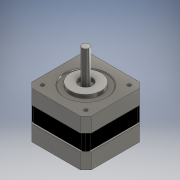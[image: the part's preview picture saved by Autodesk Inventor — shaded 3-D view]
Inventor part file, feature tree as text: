
AUTODESK INVENTOR PART (.ipt)
format: ipt  version: 2016 (Build 200138000, 138)  size: 325,632 bytes
history: native  units: mm
features: sketch x8, extrude x7, chamfer x2, other x1, fillet x1
ambient origin geometry x8: Origin, YZ Plane, XZ Plane, XY Plane, X Axis, Y Axis, Z Axis, Center Point
bodies: Solid1 (feature_tree), Body (feature_tree)
feature tree (19):
  extrude  "Raised"  Depth=42.0mm
  extrude  "Axle"  Depth=27.0mm
  extrude  "Face Indent"  Depth=27.0mm
  chamfer  "Indent Chamf"  Distance=2.5mm
  extrude  "Power Base"  Depth=2.5mm
  extrude  "Power Adapter"  Depth=33.0mm TaperAngle=0.0deg
  other  "Motor Center"
  extrude  "Coil/Winding"  Depth=22.0mm
  fillet  "Cleaner Edges"  Radius=2.0mm
  extrude  "Axle Cap"  Depth=2.0mm
  chamfer  "Cleaner Back Axle"  Distance=22.0mm
  sketch  "Sketch1"  dims[d0=42.0mm d1=42.0mm]
  sketch  "Sketch2"  dims[d2=27.0mm d3=27.0mm]
  sketch  "Sketch3"  dims[d4=27.0mm d5=27.0mm]
  sketch  "Sketch4"  dims[d18=34.367532mm]
  sketch  "Sketch5"  dims[d19=30.75mm]
  sketch  "Sketch6"  dims[d20=30.75mm]
  sketch  "Sketch7"  dims[d21=2.5mm]
  sketch  "Sketch8"  dims[d22=2.5mm d23=2.5mm d24=2.5mm d25=33.0mm d26=0.0mm d27=22.0mm d28=2.0mm d29=0.0mm d30=5.0mm d31=22.0mm d32=0.0mm d33=9.5mm d34=30.0mm d35=2.5mm d36=0.0mm d37=0.5mm d38=2.0mm d39=45.0deg d40=8.0mm d41=11.25mm d42=16.0mm d43=3.75mm d44=0.0mm d45=6.4mm d48=1.0mm d49=1.0mm d50=1.0mm d51=0.5mm d52=4.0mm d53=4.0mm d59=1.571429mm d60=0.5mm d61=1.571429mm d62=0.5mm d63=1.571429mm d64=0.5mm d65=1.571429mm d66=0.5mm d67=1.571429mm d68=0.5mm d69=1.571429mm d70=0.5mm d71=0.5mm d72=0.5mm d73=0.5mm d74=0.5mm d75=0.5mm d76=0.5mm d77=0.5mm d78=0.5mm d79=0.5mm d80=0.5mm d81=2.571429mm d82=3.2mm d83=1.0mm d84=3.2mm d85=3.2mm d86=2.25mm d87=0.0mm d88=40.0mm d89=40.0mm d90=42.0mm d91=42.0mm d92=6.0mm d93=5.25mm d94=0.0mm d95=0.0mm d96=3.0mm d97=9.5mm d98=3.0mm d99=0.0mm d100=0.5mm d101=2.0mm d102=45.0deg]
